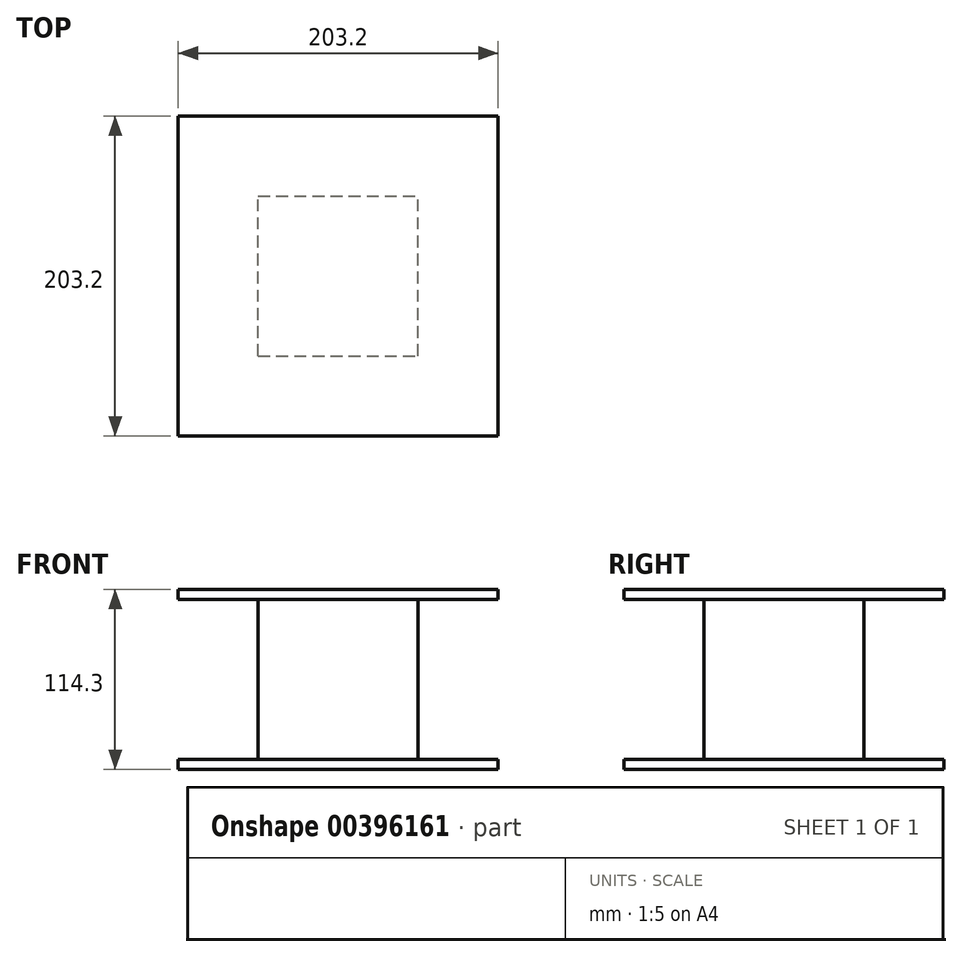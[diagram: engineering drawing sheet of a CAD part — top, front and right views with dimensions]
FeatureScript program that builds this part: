
annotation { "Feature Type Name" : "Feature", "Feature Type Description" : "" }
export const myFeature = defineFeature(function(context is Context, id is Id, definition is map)
    precondition{}
    {
        {
            var Q0;
            Q0=qCreatedBy(makeId("Front.planeOp"),FACE);
            var sketch = newSketch(context, id + "F0", { "sketchPlane" : qUnion([Q0])});
            skLineSegment(sketch, "E0.bottom", {"start": v(-50.8, -50.8) * mm, "end": v(50.8, -50.8) * mm});
            skLineSegment(sketch, "E0.top", {"start": v(-50.8, 50.8) * mm, "end": v(50.8, 50.8) * mm});
            skLineSegment(sketch, "E0.left", {"start": v(-50.8, -50.8) * mm, "end": v(-50.8, 50.8) * mm});
            skLineSegment(sketch, "E0.right", {"start": v(50.8, -50.8) * mm, "end": v(50.8, 50.8) * mm});
            skPoint(sketch, "E0.middle", {"position": v(0, 0) * mm});
            skLineSegment(sketch, "E1.bottom", {"start": v(-101.6, -57.15) * mm, "end": v(101.6, -57.15) * mm});
            skLineSegment(sketch, "E1.top", {"start": v(-101.6, -50.8) * mm, "end": v(101.6, -50.8) * mm});
            skLineSegment(sketch, "E1.left", {"start": v(-101.6, -57.15) * mm, "end": v(-101.6, -50.8) * mm});
            skLineSegment(sketch, "E1.right", {"start": v(101.6, -57.15) * mm, "end": v(101.6, -50.8) * mm});
            skPoint(sketch, "E1.middle", {"position": v(0, -53.98) * mm});
            skLineSegment(sketch, "E2.bottom", {"start": v(-101.6, 50.8) * mm, "end": v(101.6, 50.8) * mm});
            skLineSegment(sketch, "E2.top", {"start": v(-101.6, 57.15) * mm, "end": v(101.6, 57.15) * mm});
            skLineSegment(sketch, "E2.left", {"start": v(-101.6, 50.8) * mm, "end": v(-101.6, 57.15) * mm});
            skLineSegment(sketch, "E2.right", {"start": v(101.6, 50.8) * mm, "end": v(101.6, 57.15) * mm});
            skPoint(sketch, "E2.middle", {"position": v(0, 53.98) * mm});
            skPoint(sketch, "E2.middle.positionSnap0", {"position": v(0, 50.8) * mm});
            skPoint(sketch, "E2.centerSnap0", {"position": v(0, 50.8) * mm});
            skSolve(sketch);
        }
        {
            var Q0;
            Q0=makeQuery(id+"F0.imprint","IMPRINT",FACE,{"disambiguationData":[TD([[makeQuery(id+"F0.imprint","IMPRINT",EDGE,{"derivedFrom":sQuery(id+"F0.wireOp",EDGE,"E2.top")}),-1.0]])]});
            extrude(context, id + "F1", {"entities" : qUnion([Q0]), "depth" : 101.6 * mm, "hasSecondDirection" : true, "secondDirectionOppositeDirection" : true, "secondDirectionDepth" : 101.6 * mm});
        }
        {
            var Q0;
            Q0=makeQuery(id+"F0.imprint","IMPRINT",FACE,{"disambiguationData":[TD([[makeQuery(id+"F0.imprint","IMPRINT",EDGE,{"derivedFrom":sQuery(id+"F0.wireOp",EDGE,"E1.bottom")}),1.0]])]});
            extrude(context, id + "F2", {"entities" : qUnion([Q0]), "depth" : 101.6 * mm, "hasSecondDirection" : true, "secondDirectionOppositeDirection" : true, "secondDirectionDepth" : 101.6 * mm});
        }
        {
            var Q0;
            {var subQ0=sQuery(id+"F0.wireOp",EDGE,"E0.left");Q0=makeQuery(id+"F0.imprint","IMPRINT",FACE,{"disambiguationData":[TD([[makeQuery(id+"F0.imprint","IMPRINT",EDGE,{"derivedFrom":subQ0}),-1.0]])]});}
            extrude(context, id + "F3", {"entities" : qUnion([Q0]), "depth" : 50.8 * mm, "hasSecondDirection" : true, "secondDirectionOppositeDirection" : true, "secondDirectionDepth" : 50.8 * mm});
        }
    });
